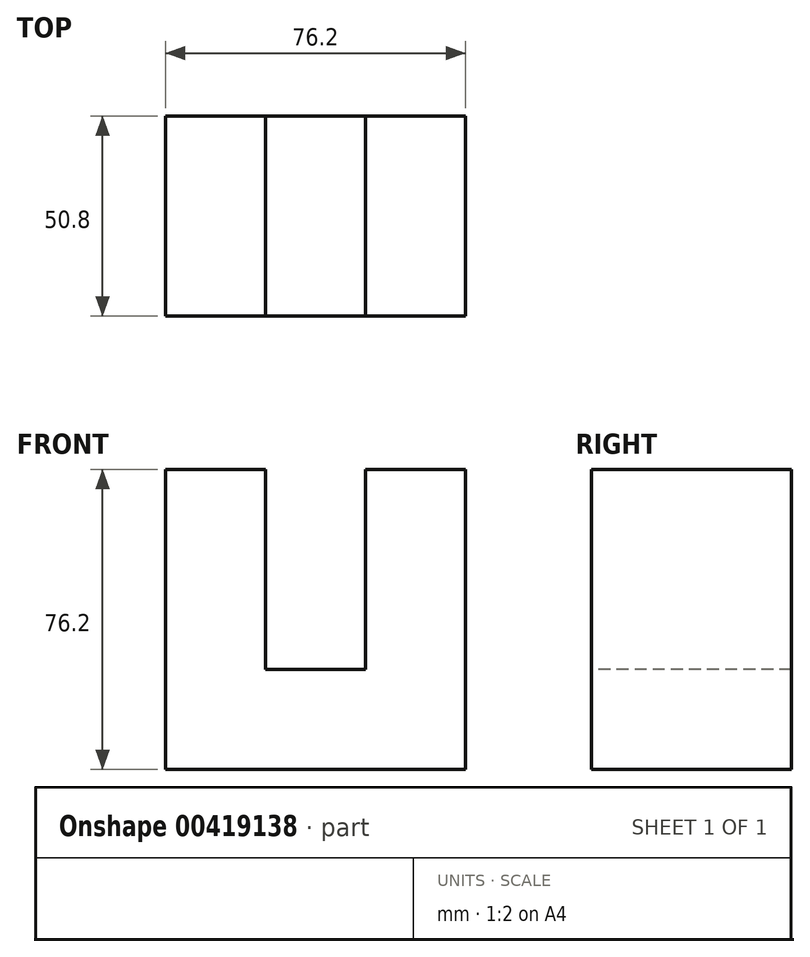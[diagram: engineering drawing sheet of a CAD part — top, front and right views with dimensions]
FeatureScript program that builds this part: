
annotation { "Feature Type Name" : "Feature", "Feature Type Description" : "" }
export const myFeature = defineFeature(function(context is Context, id is Id, definition is map)
    precondition{}
    {
        {
            var Q0;
            Q0=qCreatedBy(makeId("Front.planeOp"),FACE);
            var sketch = newSketch(context, id + "F0", { "sketchPlane" : qUnion([Q0])});
            skLineSegment(sketch, "E0", {"start": v(39.81, 0) * mm, "end": v(-36.39, 0) * mm});
            skLineSegment(sketch, "E1", {"start": v(-36.39, 0) * mm, "end": v(-36.39, 50.8) * mm});
            skLineSegment(sketch, "E2", {"start": v(-36.39, 50.8) * mm, "end": v(-36.39, 76.2) * mm});
            skLineSegment(sketch, "E3", {"start": v(-36.39, 76.2) * mm, "end": v(-10.99, 76.2) * mm});
            skLineSegment(sketch, "E4", {"start": v(-10.99, 76.2) * mm, "end": v(-10.99, 25.4) * mm});
            skLineSegment(sketch, "E5", {"start": v(-10.99, 25.4) * mm, "end": v(14.41, 25.4) * mm});
            skLineSegment(sketch, "E6", {"start": v(14.41, 25.4) * mm, "end": v(14.41, 76.2) * mm});
            skLineSegment(sketch, "E7", {"start": v(14.41, 76.2) * mm, "end": v(39.81, 76.2) * mm});
            skLineSegment(sketch, "E8", {"start": v(39.81, 76.2) * mm, "end": v(39.81, 0) * mm});
            skSolve(sketch);
        }
        {
            var Q0;
            Q0 = qSketchRegion(id + "F0", true);
            extrude(context, id + "F1", {"entities" : qUnion([Q0]), "oppositeDirection" : true, "depth" : 50.8 * mm});
        }
    });
